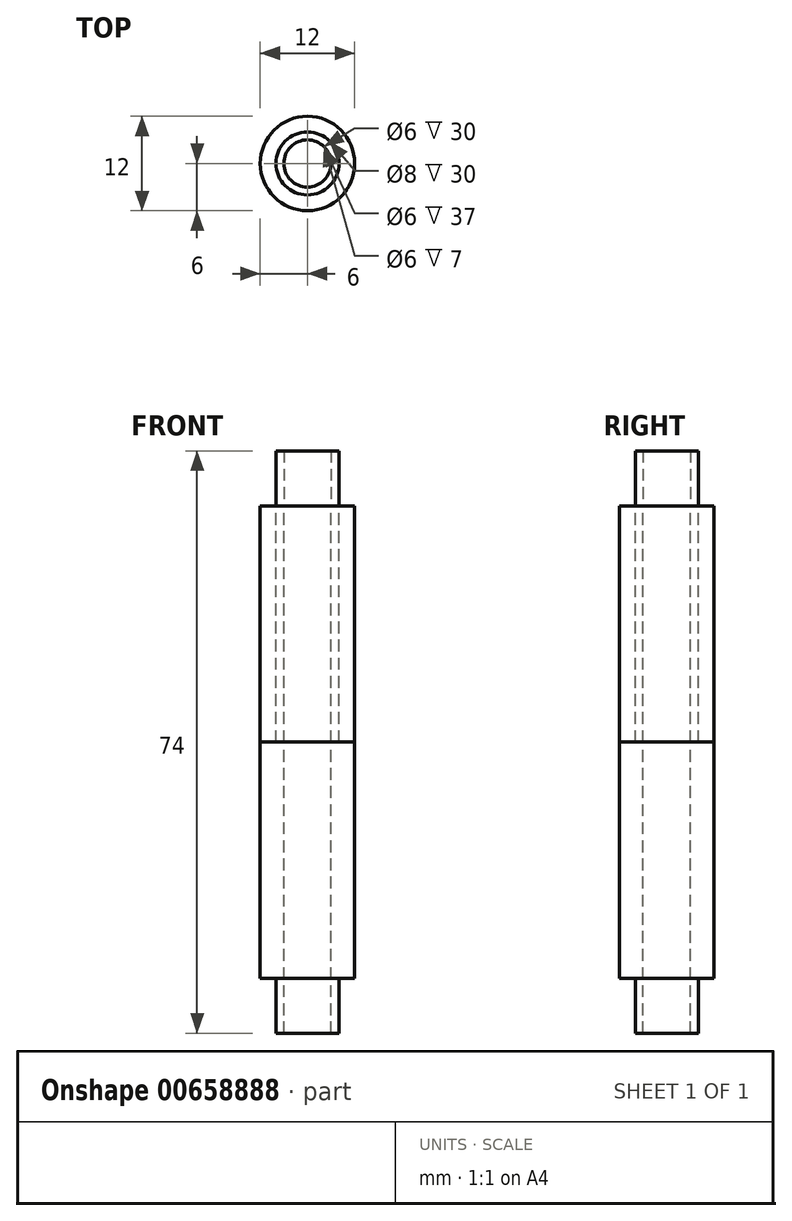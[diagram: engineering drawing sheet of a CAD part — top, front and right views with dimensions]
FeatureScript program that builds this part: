
annotation { "Feature Type Name" : "Feature", "Feature Type Description" : "" }
export const myFeature = defineFeature(function(context is Context, id is Id, definition is map)
    precondition{}
    {
        {
            var Q0;
            Q0=qCreatedBy(makeId("Top.planeOp"),FACE);
            var sketch = newSketch(context, id + "F0", { "sketchPlane" : qUnion([Q0])});
            skPoint(sketch, "E0.middle", {"position": v(0, 0) * mm});
            skCircle(sketch, "E1", {"center": v(0, 0) * mm, "radius": 4 * mm});
            skCircle(sketch, "E2", {"center": v(0, 0) * mm, "radius": 3 * mm});
            skCircle(sketch, "E3", {"center": v(0, 0) * mm, "radius": 6 * mm});
            skSolve(sketch);
        }
        {
            var Q0;
            Q0=makeQuery(id+"F0.imprint","IMPRINT",FACE,{"disambiguationData":[TD([[makeQuery(id+"F0.imprint","IMPRINT",EDGE,{"derivedFrom":sQuery(id+"F0.wireOp",EDGE,"E1")}),1.0]])]});
            extrude(context, id + "F1", {"entities" : qUnion([Q0]), "depth" : 7 * mm, "offsetDistance" : 25 * mm});
        }
        {
            var Q0;
            Q0 = qSketchRegion(id + "F0", true);
            var Q1;
            Q1=makeQuery(id+"F1.opExtrude","CAP_FACE",FACE,{"disambiguationData":[OSD([sQuery(id+"F0.wireOp",EDGE,"E1"),sQuery(id+"F0.wireOp",EDGE,"E2")])],"isStart":true});
            extrude(context, id + "F2", {"entities" : qUnion([Q0, Q1]), "oppositeDirection" : true, "depth" : 30 * mm, "offsetDistance" : 25 * mm});
        }
        {
            var Q0;
            Q0=makeQuery(id+"F2.opExtrude","CAP_FACE",FACE,{"disambiguationData":[OSD([sQuery(id+"F0.wireOp",EDGE,"E1"),sQuery(id+"F0.wireOp",EDGE,"E2")])],"isStart":false});
            var Q1;
            Q1=makeQuery(id+"F2.opExtrude","CAP_FACE",FACE,{"disambiguationData":[OSD([sQuery(id+"F0.wireOp",EDGE,"E1"),sQuery(id+"F0.wireOp",EDGE,"E3")])],"isStart":false});
            extrude(context, id + "F3", {"entities" : qUnion([Q0, Q1]), "depth" : 30 * mm, "offsetDistance" : 25 * mm});
        }
        {
            var Q0;
            Q0=makeQuery(id+"F3.opExtrude","CAP_FACE",FACE,{"disambiguationData":[OSD([sQuery(id+"F0.wireOp",EDGE,"E1"),sQuery(id+"F0.wireOp",EDGE,"E2")])],"isStart":false});
            extrude(context, id + "F4", {"entities" : qUnion([Q0]), "operationType" : NewBodyOperationType.ADD, "depth" : 7 * mm, "offsetDistance" : 25 * mm});
        }
    });
